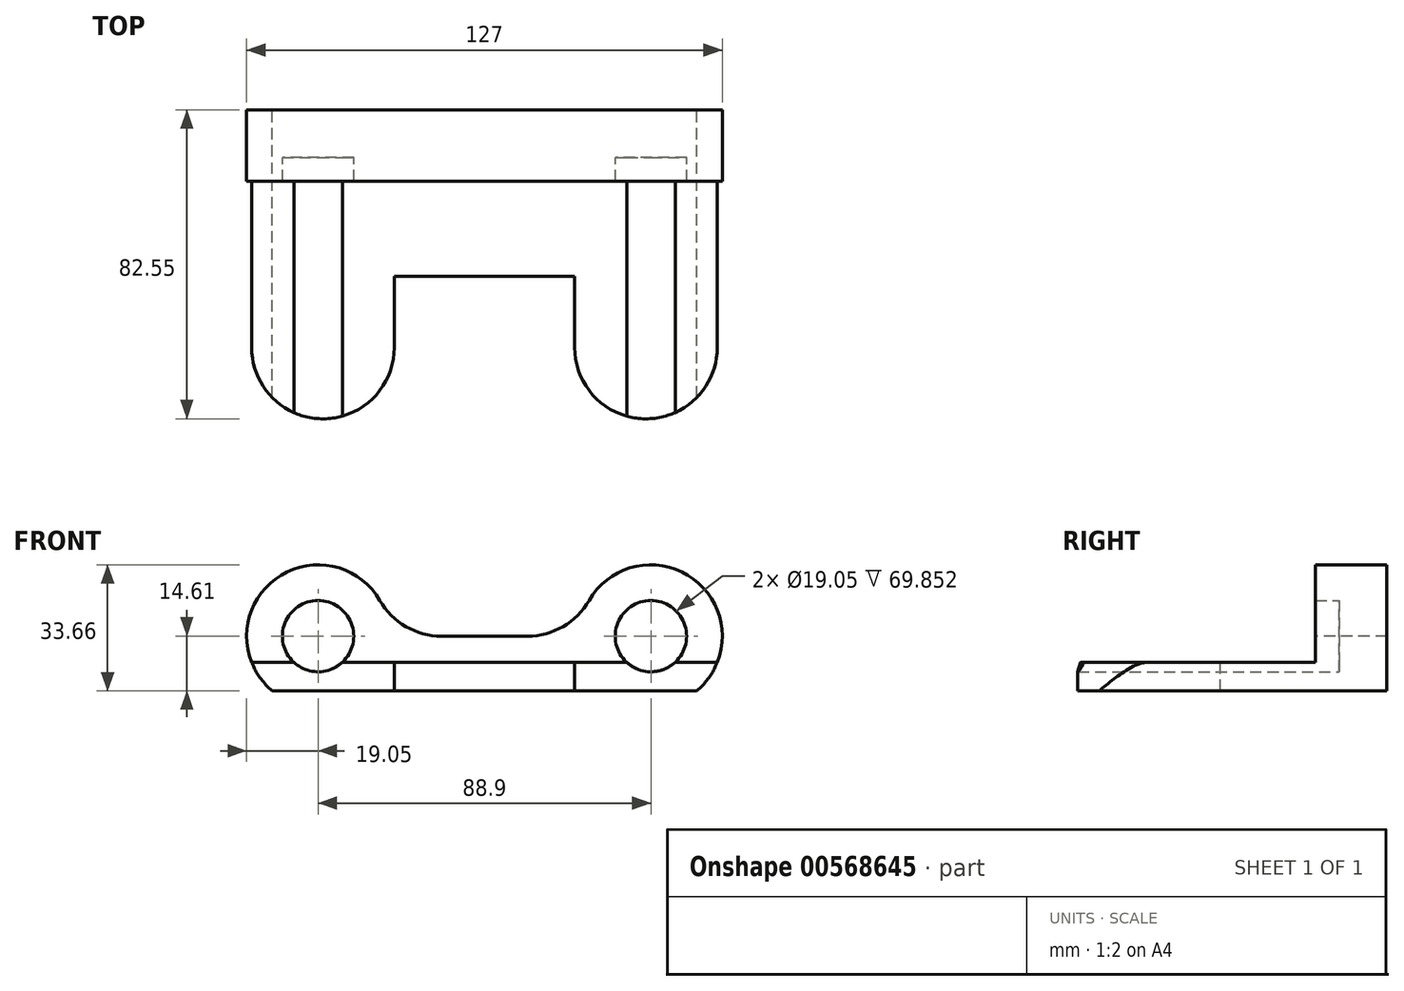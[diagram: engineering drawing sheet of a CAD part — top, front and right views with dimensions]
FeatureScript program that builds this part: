
annotation { "Feature Type Name" : "Feature", "Feature Type Description" : "" }
export const myFeature = defineFeature(function(context is Context, id is Id, definition is map)
    precondition{}
    {
        {
            var Q0;
            Q0=qCreatedBy(makeId("Front.planeOp"),FACE);
            var sketch = newSketch(context, id + "F0", { "sketchPlane" : qUnion([Q0])});
            skLineSegment(sketch, "E0.bottom", {"start": v(63.5, -19.05) * mm, "end": v(-63.5, -19.05) * mm});
            skLineSegment(sketch, "E0.top", {"start": v(63.5, 19.05) * mm, "end": v(-63.5, 19.05) * mm});
            skLineSegment(sketch, "E0.left", {"start": v(63.5, -19.05) * mm, "end": v(63.5, 19.05) * mm});
            skLineSegment(sketch, "E0.right", {"start": v(-63.5, -19.05) * mm, "end": v(-63.5, 19.05) * mm});
            skPoint(sketch, "E0.middle", {"position": v(0, 0) * mm});
            skCircle(sketch, "E1", {"center": v(-44.45, 0) * mm, "radius": 9.53 * mm});
            skCircle(sketch, "E2", {"center": v(44.45, 0) * mm, "radius": 9.53 * mm});
            skCircle(sketch, "E3", {"center": v(44.45, 0) * mm, "radius": 19.05 * mm});
            skCircle(sketch, "E4", {"center": v(-44.45, 0) * mm, "radius": 19.05 * mm});
            skLineSegment(sketch, "E5", {"start": v(25.4, 0) * mm, "end": v(-25.4, 0) * mm});
            skSolve(sketch);
        }
        {
            var Q0;
            {var subQ5=sQuery(id+"F0.wireOp",EDGE,"E5");Q0=makeQuery(id+"F0.imprint","IMPRINT",FACE,{"disambiguationData":[TD([[makeQuery(id+"F0.imprint","IMPRINT",EDGE,{"derivedFrom":subQ5}),1.0]])]});}
            var Q1;
            Q1=makeQuery(id+"F0.imprint","IMPRINT",FACE,{"disambiguationData":[TD([[makeQuery(id+"F0.imprint","IMPRINT",EDGE,{"derivedFrom":sQuery(id+"F0.wireOp",EDGE,"E1")}),-1.0]])]});
            var Q2;
            Q2=makeQuery(id+"F0.imprint","IMPRINT",FACE,{"disambiguationData":[TD([[makeQuery(id+"F0.imprint","IMPRINT",EDGE,{"derivedFrom":sQuery(id+"F0.wireOp",EDGE,"E2")}),-1.0]])]});
            extrude(context, id + "F1", {"entities" : qUnion([Q0, Q1, Q2]), "depth" : 25.4 * mm, "offsetDistance" : 25.4 * mm});
        }
        {
            var Q0;
            Q0=makeQuery(id+"F1.opExtrude","CAP_FACE",FACE,{"disambiguationData":[OSD([sQuery(id+"F0.wireOp",EDGE,"E0.bottom"),sQuery(id+"F0.wireOp",EDGE,"E1"),sQuery(id+"F0.wireOp",EDGE,"E2"),sQuery(id+"F0.wireOp",EDGE,"E3"),sQuery(id+"F0.wireOp",EDGE,"E4"),sQuery(id+"F0.wireOp",EDGE,"E5")])],"isStart":false});
            var sketch = newSketch(context, id + "F2", { "sketchPlane" : qUnion([Q0])});
            skLineSegment(sketch, "E6", {"start": v(-62.17, -6.99) * mm, "end": v(62.17, -6.99) * mm});
            skLineSegment(sketch, "E7", {"start": v(-56.68, -14.6) * mm, "end": v(56.68, -14.6) * mm});
            skSolve(sketch);
        }
        {
            var Q0;
            Q0 = qSketchRegion(id + "F2", true);
            var Q1;
            {var subQ11=sQuery(id+"F2.wireOp",EDGE,"E7");Q1=makeQuery(id+"F2.imprint","IMPRINT",FACE,{"disambiguationData":[TD([[makeQuery(id+"F2.imprint","IMPRINT",EDGE,{"derivedFrom":subQ11}),1.0]])]});}
            extrude(context, id + "F3", {"entities" : qUnion([Q0, Q1]), "operationType" : NewBodyOperationType.ADD, "depth" : 63.5 * mm, "offsetDistance" : 25.4 * mm});
        }
        {
            var Q0;
            {var subQ0=sQuery(id+"F0.wireOp",EDGE,"E4");var subQ1=sQuery(id+"F0.wireOp",EDGE,"E3");var subQ2=sQuery(id+"F0.wireOp",EDGE,"E0.bottom");Q0=makeQuery(id+"F3.boolean.opBoolean","SPLIT",FACE,{"disambiguationData":[TD([makeQuery(id+"F1.opExtrude","SWEPT_FACE",FACE,{"disambiguationData":[OSD([subQ2])]})])],"derivedFrom":makeQuery(id+"F1.opExtrude","CAP_FACE",FACE,{"disambiguationData":[OSD([subQ2,sQuery(id+"F0.wireOp",EDGE,"E1"),sQuery(id+"F0.wireOp",EDGE,"E2"),subQ1,subQ0,sQuery(id+"F0.wireOp",EDGE,"E5")])],"isStart":false})});}
            extrude(context, id + "F4", {"entities" : qUnion([Q0]), "operationType" : NewBodyOperationType.REMOVE, "oppositeDirection" : true, "depth" : 46.23 * mm, "offsetDistance" : 25.4 * mm});
        }
        {
            var Q0;
            Q0=makeQuery(id+"F1.opExtrude","SWEPT_EDGE",EDGE,{"disambiguationData":[OSD([sQuery(id+"F0.wireOp",EDGE,"E4"),sQuery(id+"F0.wireOp",EDGE,"E5")])]});
            var Q1;
            Q1=makeQuery(id+"F1.opExtrude","SWEPT_EDGE",EDGE,{"disambiguationData":[OSD([sQuery(id+"F0.wireOp",EDGE,"E3"),sQuery(id+"F0.wireOp",EDGE,"E5")])]});
            fillet(context, id + "F5", {"entities" : qUnion([Q0, Q1]), "radius" : 19.05 * mm, "tangentPropagation" : true, "allowEdgeOverflow" : false});
        }
        {
            var Q0;
            Q0=makeQuery(id+"F1.opExtrude","CAP_FACE",FACE,{"disambiguationData":[OSD([sQuery(id+"F0.wireOp",EDGE,"E0.bottom"),sQuery(id+"F0.wireOp",EDGE,"E1"),sQuery(id+"F0.wireOp",EDGE,"E2"),sQuery(id+"F0.wireOp",EDGE,"E3"),sQuery(id+"F0.wireOp",EDGE,"E4"),sQuery(id+"F0.wireOp",EDGE,"E5")])],"isStart":true});
            var sketch = newSketch(context, id + "F6", { "sketchPlane" : qUnion([Q0])});
            skCircle(sketch, "E8", {"center": v(-44.45, 0) * mm, "radius": 9.53 * mm});
            skCircle(sketch, "E9", {"center": v(44.45, 0) * mm, "radius": 9.53 * mm});
            skSolve(sketch);
        }
        {
            var Q0;
            Q0 = qSketchRegion(id + "F6", true);
            extrude(context, id + "F7", {"entities" : qUnion([Q0]), "operationType" : NewBodyOperationType.ADD, "oppositeDirection" : true, "depth" : 19.05 * mm, "offsetDistance" : 25.4 * mm});
        }
        {
            var Q0;
            Q0=makeQuery(id+"F7.boolean.opBoolean","MERGE",FACE,{"derivedFrom":[makeQuery(id+"F1.opExtrude","CAP_FACE",FACE,{"disambiguationData":[OSD([sQuery(id+"F0.wireOp",EDGE,"E0.bottom"),sQuery(id+"F0.wireOp",EDGE,"E1"),sQuery(id+"F0.wireOp",EDGE,"E2"),sQuery(id+"F0.wireOp",EDGE,"E3"),sQuery(id+"F0.wireOp",EDGE,"E4"),sQuery(id+"F0.wireOp",EDGE,"E5")])],"isStart":true}),makeQuery(id+"F7.opExtrude","CAP_FACE",FACE,{"disambiguationData":[OSD([sQuery(id+"F6.wireOp",EDGE,"E8")])],"isStart":true}),makeQuery(id+"F7.opExtrude","CAP_FACE",FACE,{"disambiguationData":[OSD([sQuery(id+"F6.wireOp",EDGE,"E9")])],"isStart":true})]});
            extrude(context, id + "F8", {"entities" : qUnion([Q0]), "operationType" : NewBodyOperationType.REMOVE, "oppositeDirection" : true, "depth" : 6.35 * mm, "offsetDistance" : 25.4 * mm});
        }
        {
            var Q0;
            {var subQ0=sQuery(id+"F2.wireOp",EDGE,"E6");Q0=makeQuery(id+"F3.opExtrude","SWEPT_FACE",FACE,{"disambiguationData":[OSD([subQ0]),TDD([makeQuery(id+"F2.imprint","IMPRINT",EDGE,{"disambiguationData":[TD([[makeQuery(id+"F2.imprint","INTERSECT",VERTEX,{"disambiguationData":[OD(1.0)],"derivedFrom":[makeQuery(id+"F1.opExtrude","CAP_EDGE",EDGE,{"disambiguationData":[OSD([sQuery(id+"F0.wireOp",EDGE,"E1")])],"isStart":false}),subQ0]}),-1.0]])],"derivedFrom":subQ0})])]});}
            var sketch = newSketch(context, id + "F9", { "sketchPlane" : qUnion([Q0])});
            skLineSegment(sketch, "E10.bottom", {"start": v(24.07, -50.8) * mm, "end": v(-24.07, -50.8) * mm});
            skLineSegment(sketch, "E10.top", {"start": v(24.07, -117.98) * mm, "end": v(-24.07, -117.98) * mm});
            skLineSegment(sketch, "E10.left", {"start": v(24.07, -50.8) * mm, "end": v(24.07, -117.98) * mm});
            skLineSegment(sketch, "E10.right", {"start": v(-24.07, -50.8) * mm, "end": v(-24.07, -117.98) * mm});
            skCircle(sketch, "E11", {"center": v(-43.12, -69.85) * mm, "radius": 19.05 * mm});
            skCircle(sketch, "E12", {"center": v(43.12, -69.85) * mm, "radius": 19.05 * mm});
            skSolve(sketch);
        }
        {
            var Q0;
            {var subQ5=sQuery(id+"F9.wireOp",EDGE,"E10.bottom");Q0=makeQuery(id+"F9.imprint","IMPRINT",FACE,{"disambiguationData":[TD([[makeQuery(id+"F9.imprint","IMPRINT",EDGE,{"derivedFrom":subQ5}),1.0]])]});}
            extrude(context, id + "F10", {"entities" : qUnion([Q0]), "operationType" : NewBodyOperationType.REMOVE, "oppositeDirection" : true, "depth" : 25.4 * mm, "offsetDistance" : 25.4 * mm});
        }
        {
            var Q0;
            {var subQ0=sQuery(id+"F2.wireOp",EDGE,"E6");var subQ1=sQuery(id+"F0.wireOp",EDGE,"E1");var subQ3=sQuery(id+"F0.wireOp",EDGE,"E2");var subQ4=sQuery(id+"F0.wireOp",EDGE,"E4");var subQ5=sQuery(id+"F2.wireOp",EDGE,"E7");Q0=makeQuery(id+"F10.boolean.opBoolean","SPLIT",FACE,{"disambiguationData":[TD([makeQuery(id+"F1.opExtrude","SWEPT_FACE",FACE,{"disambiguationData":[OSD([subQ1])]})])],"derivedFrom":makeQuery(id+"F3.opExtrude","CAP_FACE",FACE,{"disambiguationData":[OSD([subQ1,subQ3,sQuery(id+"F0.wireOp",EDGE,"E3"),subQ4,subQ0,subQ5])],"isStart":false})});}
            var sketch = newSketch(context, id + "F11", { "sketchPlane" : qUnion([Q0])});
            skLineSegment(sketch, "E13.bottom", {"start": v(-51.94, -11.62) * mm, "end": v(-34.64, -11.62) * mm});
            skLineSegment(sketch, "E13.top", {"start": v(-51.94, -6.99) * mm, "end": v(-34.64, -6.99) * mm});
            skLineSegment(sketch, "E13.left", {"start": v(-51.94, -11.62) * mm, "end": v(-51.94, -6.99) * mm});
            skLineSegment(sketch, "E13.right", {"start": v(-34.64, -11.62) * mm, "end": v(-34.64, -6.99) * mm});
            skSolve(sketch);
        }
        {
            var Q0;
            Q0 = qSketchRegion(id + "F11", true);
            extrude(context, id + "F12", {"entities" : qUnion([Q0]), "operationType" : NewBodyOperationType.ADD, "oppositeDirection" : true, "depth" : 12.7 * mm, "offsetDistance" : 25.4 * mm});
        }
        {
            var Q0;
            {var subQ0=sQuery(id+"F2.wireOp",EDGE,"E6");var subQ1=sQuery(id+"F0.wireOp",EDGE,"E3");var subQ2=sQuery(id+"F0.wireOp",EDGE,"E2");var subQ4=sQuery(id+"F0.wireOp",EDGE,"E1");var subQ5=sQuery(id+"F2.wireOp",EDGE,"E7");Q0=makeQuery(id+"F10.boolean.opBoolean","SPLIT",FACE,{"disambiguationData":[TD([makeQuery(id+"F1.opExtrude","SWEPT_FACE",FACE,{"disambiguationData":[OSD([subQ2])]})])],"derivedFrom":makeQuery(id+"F3.opExtrude","CAP_FACE",FACE,{"disambiguationData":[OSD([subQ4,subQ2,subQ1,sQuery(id+"F0.wireOp",EDGE,"E4"),subQ0,subQ5])],"isStart":false})});}
            var sketch = newSketch(context, id + "F13", { "sketchPlane" : qUnion([Q0])});
            skLineSegment(sketch, "E14.bottom", {"start": v(31.02, -6.99) * mm, "end": v(54.3, -6.99) * mm});
            skLineSegment(sketch, "E14.top", {"start": v(31.02, -12.4) * mm, "end": v(54.3, -12.4) * mm});
            skLineSegment(sketch, "E14.left", {"start": v(31.02, -6.99) * mm, "end": v(31.02, -12.4) * mm});
            skLineSegment(sketch, "E14.right", {"start": v(54.3, -6.99) * mm, "end": v(54.3, -12.4) * mm});
            skSolve(sketch);
        }
        {
            var Q0;
            Q0 = qSketchRegion(id + "F13", true);
            extrude(context, id + "F14", {"entities" : qUnion([Q0]), "operationType" : NewBodyOperationType.ADD, "oppositeDirection" : true, "depth" : 12.7 * mm, "offsetDistance" : 25.4 * mm});
        }
        {
            var Q0;
            {var subQ0=sQuery(id+"F2.wireOp",EDGE,"E6");var subQ1=makeQuery(id+"F1.opExtrude","CAP_EDGE",EDGE,{"disambiguationData":[OSD([sQuery(id+"F0.wireOp",EDGE,"E1")])],"isStart":false});Q0=makeQuery(id+"F14.boolean.opBoolean","MERGE",FACE,{"derivedFrom":[makeQuery(id+"F3.opExtrude","SWEPT_FACE",FACE,{"disambiguationData":[OSD([subQ0]),TDD([makeQuery(id+"F2.imprint","IMPRINT",EDGE,{"disambiguationData":[TD([[makeQuery(id+"F2.imprint","INTERSECT",VERTEX,{"derivedFrom":[makeQuery(id+"F1.opExtrude","CAP_EDGE",EDGE,{"disambiguationData":[OSD([sQuery(id+"F0.wireOp",EDGE,"E3")])],"isStart":false}),subQ0]}),1.0]])],"derivedFrom":subQ0})])]}),makeQuery(id+"F12.boolean.opBoolean","MERGE",FACE,{"derivedFrom":[makeQuery(id+"F3.opExtrude","SWEPT_FACE",FACE,{"disambiguationData":[OSD([subQ0]),TDD([makeQuery(id+"F2.imprint","IMPRINT",EDGE,{"disambiguationData":[TD([[makeQuery(id+"F2.imprint","INTERSECT",VERTEX,{"derivedFrom":[makeQuery(id+"F1.opExtrude","CAP_EDGE",EDGE,{"disambiguationData":[OSD([sQuery(id+"F0.wireOp",EDGE,"E4")])],"isStart":false}),subQ0]}),-1.0]])],"derivedFrom":subQ0})])]}),makeQuery(id+"F3.opExtrude","SWEPT_FACE",FACE,{"disambiguationData":[OSD([subQ0]),TDD([makeQuery(id+"F2.imprint","IMPRINT",EDGE,{"disambiguationData":[TD([[makeQuery(id+"F2.imprint","INTERSECT",VERTEX,{"disambiguationData":[OD(1.0)],"derivedFrom":[subQ1,subQ0]}),-1.0]])],"derivedFrom":subQ0})])]}),makeQuery(id+"F12.opExtrude","SWEPT_FACE",FACE,{"disambiguationData":[OSD([sQuery(id+"F11.wireOp",EDGE,"E13.top")])]})]}),makeQuery(id+"F14.opExtrude","SWEPT_FACE",FACE,{"disambiguationData":[OSD([sQuery(id+"F13.wireOp",EDGE,"E14.bottom")])]})]});}
            var sketch = newSketch(context, id + "F15", { "sketchPlane" : qUnion([Q0])});
            skCircle(sketch, "E15", {"center": v(43.12, -69.85) * mm, "radius": 19.05 * mm});
            skCircle(sketch, "E16", {"center": v(-43.12, -69.85) * mm, "radius": 19.05 * mm});
            skSolve(sketch);
        }
        {
            var Q0;
            {var subQ0=sQuery(id+"F15.wireOp",EDGE,"E15");var subQ1=sQuery(id+"F2.wireOp",EDGE,"E6");var subQ2=sQuery(id+"F0.wireOp",EDGE,"E3");var subQ3=makeQuery(id+"F3.opExtrude","SWEPT_EDGE",EDGE,{"disambiguationData":[OSD([subQ2,subQ1])]});var subQ4=makeQuery(id+"F15.imprint","INTERSECT",VERTEX,{"derivedFrom":[subQ3,subQ0]});Q0=makeQuery(id+"F15.imprint","IMPRINT",FACE,{"disambiguationData":[TD([[makeQuery(id+"F15.imprint","IMPRINT",EDGE,{"disambiguationData":[TD([[subQ4,1.0]])],"derivedFrom":subQ0}),-1.0]])]});}
            var Q1;
            {var subQ0=sQuery(id+"F15.wireOp",EDGE,"E15");var subQ1=sQuery(id+"F9.wireOp",EDGE,"E10.left");var subQ2=makeQuery(id+"F10.boolean.opBoolean","COPY",EDGE,{"derivedFrom":makeQuery(id+"F10.opExtrude","CAP_EDGE",EDGE,{"disambiguationData":[OSD([subQ1])],"isStart":true})});var subQ3=makeQuery(id+"F15.imprint","INTERSECT",VERTEX,{"derivedFrom":[subQ2,subQ0]});Q1=makeQuery(id+"F15.imprint","IMPRINT",FACE,{"disambiguationData":[TD([[makeQuery(id+"F15.imprint","IMPRINT",EDGE,{"disambiguationData":[TD([[subQ3,-1.0]])],"derivedFrom":subQ0}),-1.0]])]});}
            var Q2;
            {var subQ0=sQuery(id+"F15.wireOp",EDGE,"E16");var subQ1=sQuery(id+"F9.wireOp",EDGE,"E10.right");var subQ2=makeQuery(id+"F10.boolean.opBoolean","COPY",EDGE,{"derivedFrom":makeQuery(id+"F10.opExtrude","CAP_EDGE",EDGE,{"disambiguationData":[OSD([subQ1])],"isStart":true})});var subQ3=makeQuery(id+"F15.imprint","INTERSECT",VERTEX,{"derivedFrom":[subQ2,subQ0]});Q2=makeQuery(id+"F15.imprint","IMPRINT",FACE,{"disambiguationData":[TD([[makeQuery(id+"F15.imprint","IMPRINT",EDGE,{"disambiguationData":[TD([[subQ3,1.0]])],"derivedFrom":subQ0}),-1.0]])]});}
            var Q3;
            {var subQ0=sQuery(id+"F15.wireOp",EDGE,"E16");var subQ1=sQuery(id+"F2.wireOp",EDGE,"E6");var subQ2=sQuery(id+"F0.wireOp",EDGE,"E4");var subQ3=makeQuery(id+"F3.opExtrude","SWEPT_EDGE",EDGE,{"disambiguationData":[OSD([subQ2,subQ1])]});var subQ4=makeQuery(id+"F15.imprint","INTERSECT",VERTEX,{"derivedFrom":[subQ3,subQ0]});Q3=makeQuery(id+"F15.imprint","IMPRINT",FACE,{"disambiguationData":[TD([[makeQuery(id+"F15.imprint","IMPRINT",EDGE,{"disambiguationData":[TD([[subQ4,-1.0]])],"derivedFrom":subQ0}),-1.0]])]});}
            extrude(context, id + "F16", {"entities" : qUnion([Q0, Q1, Q2, Q3]), "operationType" : NewBodyOperationType.REMOVE, "oppositeDirection" : true, "depth" : 25.4 * mm, "offsetDistance" : 25.4 * mm});
        }
        {
            var Q0;
            Q0=makeQuery(id+"F14.opExtrude","CAP_FACE",FACE,{"disambiguationData":[OSD([sQuery(id+"F13.wireOp",EDGE,"E14.bottom"),sQuery(id+"F13.wireOp",EDGE,"E14.top"),sQuery(id+"F13.wireOp",EDGE,"E14.left"),sQuery(id+"F13.wireOp",EDGE,"E14.right")])],"isStart":false});
            var Q1;
            Q1=makeQuery(id+"F12.opExtrude","CAP_FACE",FACE,{"disambiguationData":[OSD([sQuery(id+"F11.wireOp",EDGE,"E13.bottom"),sQuery(id+"F11.wireOp",EDGE,"E13.top"),sQuery(id+"F11.wireOp",EDGE,"E13.left"),sQuery(id+"F11.wireOp",EDGE,"E13.right")])],"isStart":false});
            extrude(context, id + "F17", {"entities" : qUnion([Q0, Q1]), "operationType" : NewBodyOperationType.REMOVE, "oppositeDirection" : true, "depth" : 25.4 * mm, "offsetDistance" : 25.4 * mm});
        }
    });
